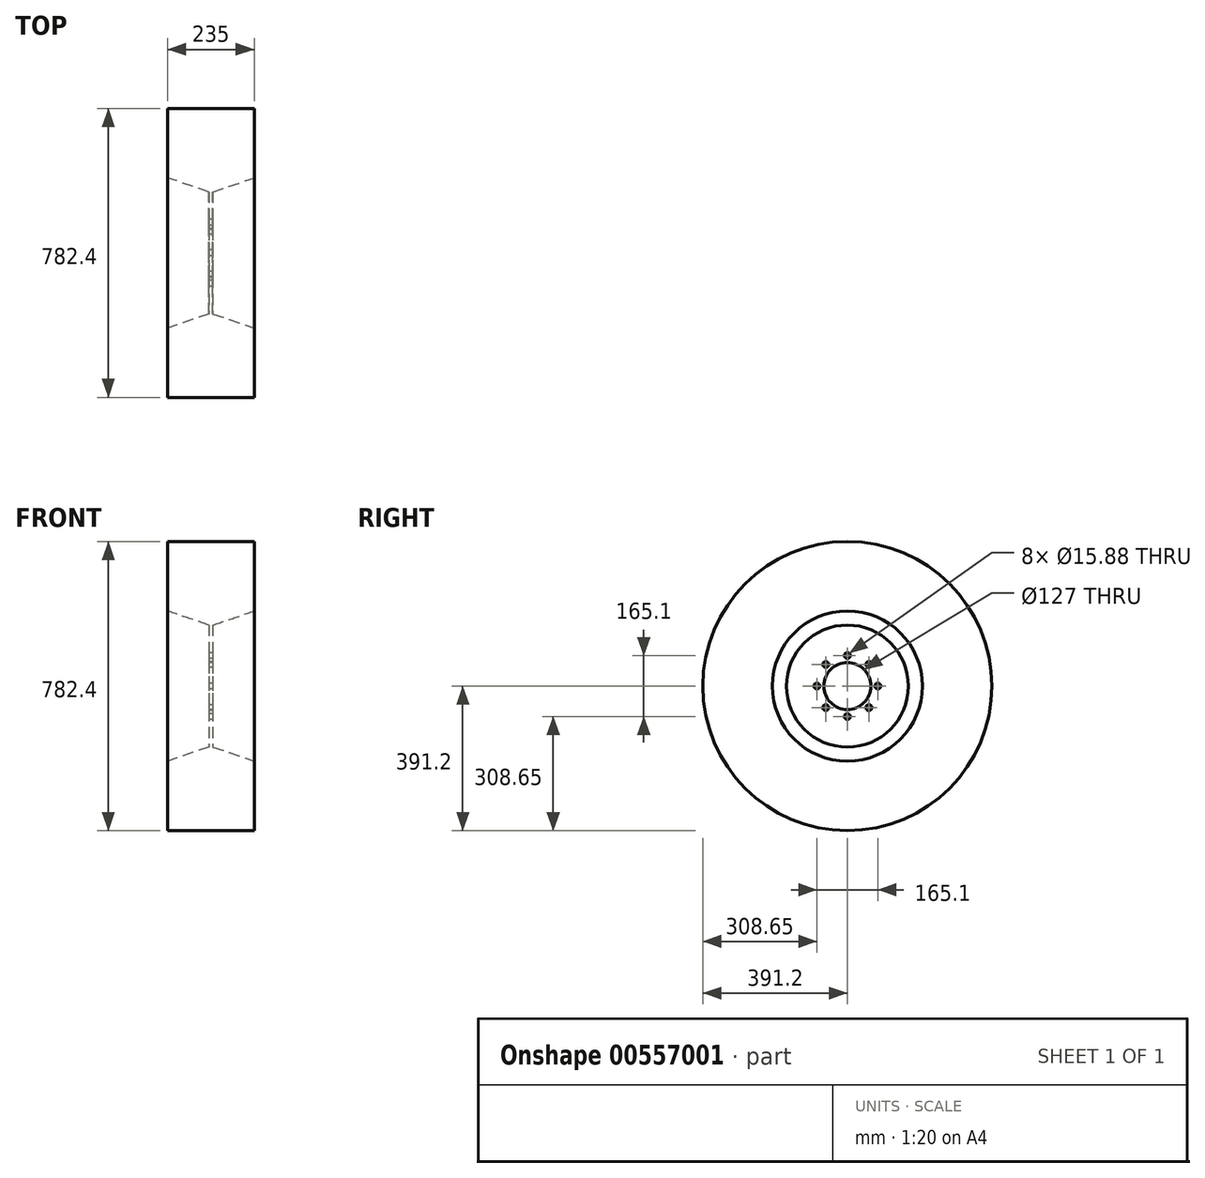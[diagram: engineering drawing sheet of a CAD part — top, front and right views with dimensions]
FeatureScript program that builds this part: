
annotation { "Feature Type Name" : "Feature", "Feature Type Description" : "" }
export const myFeature = defineFeature(function(context is Context, id is Id, definition is map)
    precondition{}
    {
        {
            var Q0;
            Q0=qCreatedBy(makeId("Front.planeOp"),FACE);
            var sketch = newSketch(context, id + "F0", { "sketchPlane" : qUnion([Q0])});
            skLineSegment(sketch, "E0", {"start": v(-5.08, 63.5) * mm, "end": v(5.08, 63.5) * mm});
            skLineSegment(sketch, "E1", {"start": v(5.08, 63.5) * mm, "end": v(5.08, 165.1) * mm});
            skLineSegment(sketch, "E2", {"start": v(5.08, 165.1) * mm, "end": v(117.5, 203.2) * mm});
            skLineSegment(sketch, "E3", {"start": v(-117.5, 203.2) * mm, "end": v(-5.08, 165.1) * mm});
            skLineSegment(sketch, "E4", {"start": v(-5.08, 165.1) * mm, "end": v(-5.08, 63.5) * mm});
            skLineSegment(sketch, "E5", {"start": v(117.5, 391.2) * mm, "end": v(-117.5, 391.2) * mm});
            skLineSegment(sketch, "E6", {"start": v(-117.5, 203.2) * mm, "end": v(-117.5, 391.2) * mm});
            skLineSegment(sketch, "E7", {"start": v(117.5, 391.2) * mm, "end": v(117.5, 203.2) * mm});
            skLineSegment(sketch, "E8", {"start": v(-118.95, 0) * mm, "end": v(140.02, 0) * mm, "construction": true});
            skSolve(sketch);
        }
        {
            var Q0;
            Q0=makeQuery(id+"F0.imprint","IMPRINT",FACE,{"disambiguationData":[TD([[makeQuery(id+"F0.imprint","IMPRINT",EDGE,{"derivedFrom":sQuery(id+"F0.wireOp",EDGE,"E0")}),1.0]])]});
            var Q1;
            Q1=sQuery(id+"F0.wireOp",EDGE,"E8");
            revolve(context, id + "F1", {"entities" : qUnion([Q0]), "axis" : qUnion([Q1]), "revolveType" : RevolveType.FULL});
        }
        {
            var Q0;
            Q0=makeQuery(id+"F1.opRevolve","SWEPT_FACE",FACE,{"disambiguationData":[OSD([sQuery(id+"F0.wireOp",EDGE,"E4")])]});
            var sketch = newSketch(context, id + "F2", { "sketchPlane" : qUnion([Q0])});
            skCircle(sketch, "E9", {"center": v(0, 82.55) * mm, "radius": 7.94 * mm});
            skCircle(sketch, "E10.1.0", {"center": v(-58.37, 58.37) * mm, "radius": 7.94 * mm});
            skCircle(sketch, "E10.2.0", {"center": v(-82.55, 0) * mm, "radius": 7.94 * mm});
            skCircle(sketch, "E10.3.0", {"center": v(-58.37, -58.37) * mm, "radius": 7.94 * mm});
            skCircle(sketch, "E10.4.0", {"center": v(0, -82.55) * mm, "radius": 7.94 * mm});
            skCircle(sketch, "E10.5.0", {"center": v(58.37, -58.37) * mm, "radius": 7.94 * mm});
            skCircle(sketch, "E10.6.0", {"center": v(82.55, 0) * mm, "radius": 7.94 * mm});
            skCircle(sketch, "E10.7.0", {"center": v(58.37, 58.37) * mm, "radius": 7.94 * mm});
            skPoint(sketch, "E10.center", {"position": v(0, 0) * mm});
            skSolve(sketch);
        }
        {
            var Q0;
            Q0=makeQuery(id+"F2.imprint","IMPRINT",FACE,{"disambiguationData":[TD([[makeQuery(id+"F2.imprint","IMPRINT",EDGE,{"derivedFrom":sQuery(id+"F2.wireOp",EDGE,"E9")}),1.0]])]});
            var Q1;
            Q1=makeQuery(id+"F2.imprint","IMPRINT",FACE,{"disambiguationData":[TD([[makeQuery(id+"F2.imprint","IMPRINT",EDGE,{"derivedFrom":sQuery(id+"F2.wireOp",EDGE,"E10.7.0")}),1.0]])]});
            var Q2;
            Q2=makeQuery(id+"F2.imprint","IMPRINT",FACE,{"disambiguationData":[TD([[makeQuery(id+"F2.imprint","IMPRINT",EDGE,{"derivedFrom":sQuery(id+"F2.wireOp",EDGE,"E10.6.0")}),1.0]])]});
            var Q3;
            Q3=makeQuery(id+"F2.imprint","IMPRINT",FACE,{"disambiguationData":[TD([[makeQuery(id+"F2.imprint","IMPRINT",EDGE,{"derivedFrom":sQuery(id+"F2.wireOp",EDGE,"E10.5.0")}),1.0]])]});
            var Q4;
            Q4=makeQuery(id+"F2.imprint","IMPRINT",FACE,{"disambiguationData":[TD([[makeQuery(id+"F2.imprint","IMPRINT",EDGE,{"derivedFrom":sQuery(id+"F2.wireOp",EDGE,"E10.4.0")}),1.0]])]});
            var Q5;
            Q5=makeQuery(id+"F2.imprint","IMPRINT",FACE,{"disambiguationData":[TD([[makeQuery(id+"F2.imprint","IMPRINT",EDGE,{"derivedFrom":sQuery(id+"F2.wireOp",EDGE,"E10.3.0")}),1.0]])]});
            var Q6;
            Q6=makeQuery(id+"F2.imprint","IMPRINT",FACE,{"disambiguationData":[TD([[makeQuery(id+"F2.imprint","IMPRINT",EDGE,{"derivedFrom":sQuery(id+"F2.wireOp",EDGE,"E10.2.0")}),1.0]])]});
            var Q7;
            Q7=makeQuery(id+"F2.imprint","IMPRINT",FACE,{"disambiguationData":[TD([[makeQuery(id+"F2.imprint","IMPRINT",EDGE,{"derivedFrom":sQuery(id+"F2.wireOp",EDGE,"E10.1.0")}),1.0]])]});
            extrude(context, id + "F3", {"entities" : qUnion([Q0, Q1, Q2, Q3, Q4, Q5, Q6, Q7]), "operationType" : NewBodyOperationType.REMOVE, "endBound" : BoundingType.THROUGH_ALL, "oppositeDirection" : true, "depth" : 25.4 * mm, "offsetDistance" : 25.4 * mm});
        }
    });
